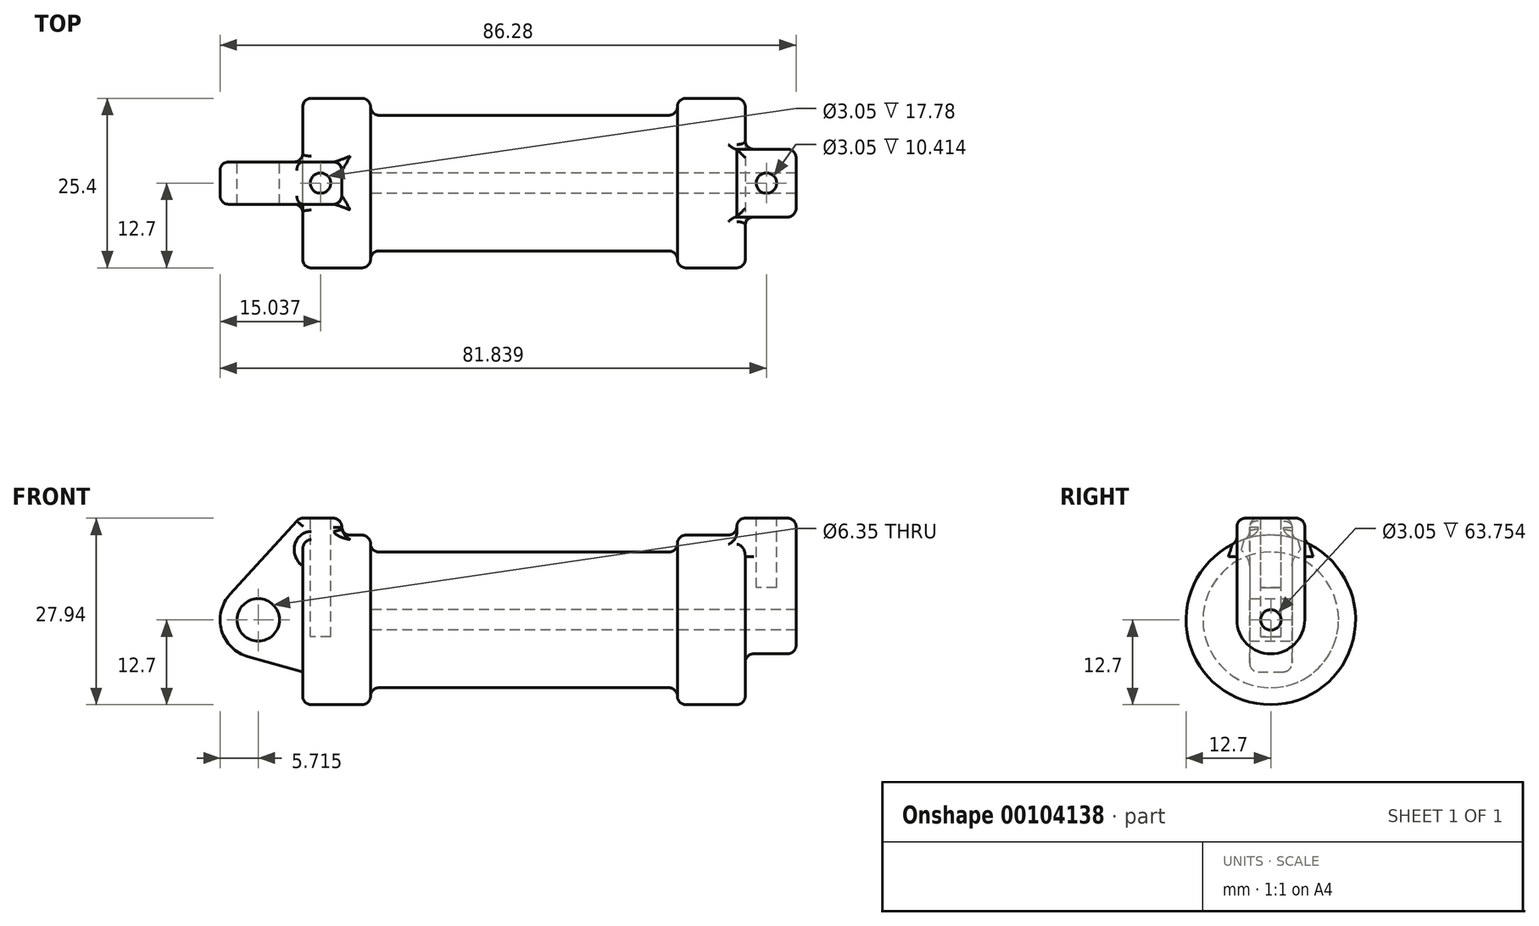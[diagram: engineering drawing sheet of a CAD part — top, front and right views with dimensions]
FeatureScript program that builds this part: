
annotation { "Feature Type Name" : "Feature", "Feature Type Description" : "" }
export const myFeature = defineFeature(function(context is Context, id is Id, definition is map)
    precondition{}
    {
        {
            var Q0;
            Q0=qCreatedBy(makeId("Front.planeOp"),FACE);
            var sketch = newSketch(context, id + "F0", { "sketchPlane" : qUnion([Q0])});
            skLineSegment(sketch, "E0", {"start": v(0, 0) * mm, "end": v(0, 12.7) * mm});
            skLineSegment(sketch, "E1", {"start": v(0, 12.7) * mm, "end": v(10.16, 12.7) * mm});
            skLineSegment(sketch, "E2", {"start": v(10.16, 12.7) * mm, "end": v(10.16, 10.16) * mm});
            skLineSegment(sketch, "E3", {"start": v(10.16, 10.16) * mm, "end": v(56.13, 10.16) * mm});
            skLineSegment(sketch, "E4", {"start": v(56.13, 10.16) * mm, "end": v(56.13, 12.7) * mm});
            skLineSegment(sketch, "E5", {"start": v(56.13, 12.7) * mm, "end": v(66.3, 12.7) * mm});
            skLineSegment(sketch, "E6", {"start": v(66.3, 12.7) * mm, "end": v(66.3, 0) * mm});
            skLineSegment(sketch, "E7", {"start": v(66.3, 0) * mm, "end": v(0, 0) * mm});
            skLineSegment(sketch, "E8", {"start": v(5.84, 15.24) * mm, "end": v(-0.5, 15.24) * mm});
            skLineSegment(sketch, "E9", {"start": v(-0.5, 15.24) * mm, "end": v(-10.88, 3.85) * mm});
            skLineSegment(sketch, "E10", {"start": v(0, 0) * mm, "end": v(-6.65, 0) * mm});
            skCircle(sketch, "E11", {"center": v(-6.65, 0) * mm, "radius": 5.72 * mm});
            skCircle(sketch, "E12", {"center": v(-6.65, 0) * mm, "radius": 3.18 * mm});
            skLineSegment(sketch, "E13", {"start": v(5.84, 15.24) * mm, "end": v(5.84, -9.4) * mm});
            skLineSegment(sketch, "E14", {"start": v(5.84, -9.4) * mm, "end": v(-8.18, -5.5) * mm});
            skSolve(sketch);
        }
        {
            var Q0;
            {var subQ0=sQuery(id+"F0.wireOp",EDGE,"E2");Q0=makeQuery(id+"F0.imprint","IMPRINT",FACE,{"disambiguationData":[TD([[makeQuery(id+"F0.imprint","IMPRINT",EDGE,{"derivedFrom":subQ0}),-1.0]])]});}
            var Q1;
            {var subQ0=sQuery(id+"F0.wireOp",EDGE,"E0");Q1=makeQuery(id+"F0.imprint","IMPRINT",FACE,{"disambiguationData":[TD([[makeQuery(id+"F0.imprint","IMPRINT",EDGE,{"derivedFrom":subQ0}),-1.0]])]});}
            var Q2;
            Q2=sQuery(id+"F0.wireOp",EDGE,"E7");
            revolve(context, id + "F1", {"entities" : qUnion([Q0, Q1]), "axis" : qUnion([Q2]), "revolveType" : RevolveType.FULL});
        }
        {
            var Q0;
            {var subQ3=sQuery(id+"F0.wireOp",EDGE,"E0");Q0=makeQuery(id+"F0.imprint","IMPRINT",FACE,{"disambiguationData":[TD([[makeQuery(id+"F0.imprint","IMPRINT",EDGE,{"derivedFrom":subQ3}),1.0]])]});}
            var Q1;
            {var subQ0=sQuery(id+"F0.wireOp",EDGE,"E0");Q1=makeQuery(id+"F0.imprint","IMPRINT",FACE,{"disambiguationData":[TD([[makeQuery(id+"F0.imprint","IMPRINT",EDGE,{"derivedFrom":subQ0}),-1.0]])]});}
            var Q2;
            {var subQ0=sQuery(id+"F0.wireOp",EDGE,"E14");Q2=makeQuery(id+"F0.imprint","IMPRINT",FACE,{"disambiguationData":[TD([[makeQuery(id+"F0.imprint","IMPRINT",EDGE,{"derivedFrom":subQ0}),-1.0]])]});}
            var Q3;
            {var subQ4=sQuery(id+"F0.wireOp",EDGE,"E12");Q3=makeQuery(id+"F0.imprint","IMPRINT",FACE,{"disambiguationData":[TD([[makeQuery(id+"F0.imprint","IMPRINT",EDGE,{"derivedFrom":subQ4}),-1.0]])]});}
            extrude(context, id + "F2", {"entities" : qUnion([Q0, Q1, Q2, Q3]), "operationType" : NewBodyOperationType.ADD, "depth" : 3.17 * mm});
        }
        {
            var Q0;
            {var subQ4=sQuery(id+"F0.wireOp",EDGE,"E12");Q0=makeQuery(id+"F0.imprint","IMPRINT",FACE,{"disambiguationData":[TD([[makeQuery(id+"F0.imprint","IMPRINT",EDGE,{"derivedFrom":subQ4}),-1.0]])]});}
            var Q1;
            {var subQ3=sQuery(id+"F0.wireOp",EDGE,"E0");Q1=makeQuery(id+"F0.imprint","IMPRINT",FACE,{"disambiguationData":[TD([[makeQuery(id+"F0.imprint","IMPRINT",EDGE,{"derivedFrom":subQ3}),1.0]])]});}
            var Q2;
            {var subQ0=sQuery(id+"F0.wireOp",EDGE,"E0");Q2=makeQuery(id+"F0.imprint","IMPRINT",FACE,{"disambiguationData":[TD([[makeQuery(id+"F0.imprint","IMPRINT",EDGE,{"derivedFrom":subQ0}),-1.0]])]});}
            var Q3;
            {var subQ0=sQuery(id+"F0.wireOp",EDGE,"E14");Q3=makeQuery(id+"F0.imprint","IMPRINT",FACE,{"disambiguationData":[TD([[makeQuery(id+"F0.imprint","IMPRINT",EDGE,{"derivedFrom":subQ0}),-1.0]])]});}
            extrude(context, id + "F3", {"entities" : qUnion([Q0, Q1, Q2, Q3]), "operationType" : NewBodyOperationType.ADD, "oppositeDirection" : true, "depth" : 3.17 * mm});
        }
        {
            var Q0;
            Q0=makeQuery(id+"F1.opRevolve","SWEPT_FACE",FACE,{"disambiguationData":[OSD([sQuery(id+"F0.wireOp",EDGE,"E6")])]});
            var sketch = newSketch(context, id + "F4", { "sketchPlane" : qUnion([Q0])});
            skCircle(sketch, "E15", {"center": v(0, 0) * mm, "radius": 5.08 * mm});
            skCircle(sketch, "E16", {"center": v(0, 0) * mm, "radius": 1.52 * mm});
            skLineSegment(sketch, "E17", {"start": v(-5.08, 0) * mm, "end": v(-5.08, 15.24) * mm});
            skLineSegment(sketch, "E18", {"start": v(-5.08, 15.24) * mm, "end": v(5.08, 15.24) * mm});
            skLineSegment(sketch, "E19", {"start": v(5.08, 15.24) * mm, "end": v(5.08, 0) * mm});
            skSolve(sketch);
        }
        {
            var Q0;
            {var subQ0=sQuery(id+"F4.wireOp",EDGE,"E18");Q0=makeQuery(id+"F4.imprint","IMPRINT",FACE,{"disambiguationData":[TD([[makeQuery(id+"F4.imprint","IMPRINT",EDGE,{"derivedFrom":subQ0}),-1.0]])]});}
            var Q1;
            {var subQ0=sQuery(id+"F4.wireOp",EDGE,"E17");var subQ1=sQuery(id+"F4.wireOp",EDGE,"E15");var subQ2=makeQuery(id+"F4.imprint","INTERSECT",VERTEX,{"derivedFrom":[subQ1,subQ0]});Q1=makeQuery(id+"F4.imprint","IMPRINT",FACE,{"disambiguationData":[TD([[makeQuery(id+"F4.imprint","IMPRINT",EDGE,{"disambiguationData":[TD([[subQ2,1.0]])],"derivedFrom":subQ1}),-1.0]])]});}
            var Q2;
            Q2=makeQuery(id+"F4.imprint","IMPRINT",FACE,{"disambiguationData":[TD([[makeQuery(id+"F4.imprint","IMPRINT",EDGE,{"derivedFrom":sQuery(id+"F4.wireOp",EDGE,"E16")}),-1.0]])]});
            extrude(context, id + "F5", {"entities" : qUnion([Q0, Q1, Q2]), "operationType" : NewBodyOperationType.ADD, "depth" : 7.62 * mm});
        }
        {
            var Q0;
            Q0=makeQuery(id+"F5.opExtrude","CAP_FACE",FACE,{"disambiguationData":[OSD([sQuery(id+"F4.wireOp",EDGE,"E15"),sQuery(id+"F4.wireOp",EDGE,"E16"),sQuery(id+"F4.wireOp",EDGE,"E17"),sQuery(id+"F4.wireOp",EDGE,"E18"),sQuery(id+"F4.wireOp",EDGE,"E19")])],"isStart":false});
            extrude(context, id + "F6", {"entities" : qUnion([Q0]), "operationType" : NewBodyOperationType.ADD, "oppositeDirection" : true, "depth" : 8.9 * mm});
        }
        {
            var Q0;
            {var subQ0=sQuery(id+"F0.wireOp",EDGE,"E8");Q0=makeQuery(id+"F3.boolean.opBoolean","MERGE",FACE,{"derivedFrom":[makeQuery(id+"F2.opExtrude","SWEPT_FACE",FACE,{"disambiguationData":[OSD([subQ0])]}),makeQuery(id+"F3.opExtrude","SWEPT_FACE",FACE,{"disambiguationData":[OSD([subQ0])]})]});}
            var sketch = newSketch(context, id + "F7", { "sketchPlane" : qUnion([Q0])});
            skCircle(sketch, "E20", {"center": v(2.67, 0) * mm, "radius": 1.52 * mm});
            skPoint(sketch, "E20.centerSnap0", {"position": v(5.84, 0) * mm});
            skLineSegment(sketch, "E21.bottom", {"start": v(-0.5, -3.18) * mm, "end": v(2.67, -3.18) * mm, "construction": true});
            skLineSegment(sketch, "E21.top", {"start": v(-0.5, 0) * mm, "end": v(2.67, 0) * mm, "construction": true});
            skLineSegment(sketch, "E21.left", {"start": v(-0.5, -3.18) * mm, "end": v(-0.5, 0) * mm, "construction": true});
            skLineSegment(sketch, "E21.right", {"start": v(2.67, -3.18) * mm, "end": v(2.67, 0) * mm, "construction": true});
            skSolve(sketch);
        }
        {
            var Q0;
            Q0=makeQuery(id+"F7.imprint","IMPRINT",FACE,{"disambiguationData":[TD([[makeQuery(id+"F7.imprint","IMPRINT",EDGE,{"derivedFrom":sQuery(id+"F7.wireOp",EDGE,"E20")}),1.0]])]});
            extrude(context, id + "F8", {"entities" : qUnion([Q0]), "operationType" : NewBodyOperationType.REMOVE, "oppositeDirection" : true, "depth" : 17.78 * mm});
        }
        {
            var Q0;
            {var subQ0=sQuery(id+"F4.wireOp",EDGE,"E18");Q0=makeQuery(id+"F6.boolean.opBoolean","MERGE",FACE,{"derivedFrom":[makeQuery(id+"F5.opExtrude","SWEPT_FACE",FACE,{"disambiguationData":[OSD([subQ0])]}),makeQuery(id+"F6.opExtrude","SWEPT_FACE",FACE,{"disambiguationData":[OSD([subQ0])]})]});}
            var sketch = newSketch(context, id + "F9", { "sketchPlane" : qUnion([Q0])});
            skLineSegment(sketch, "E22.bottom", {"start": v(65.02, -5.08) * mm, "end": v(69.47, -5.08) * mm, "construction": true});
            skLineSegment(sketch, "E22.top", {"start": v(65.02, 0) * mm, "end": v(69.47, 0) * mm, "construction": true});
            skLineSegment(sketch, "E22.left", {"start": v(65.02, -5.08) * mm, "end": v(65.02, 0) * mm, "construction": true});
            skLineSegment(sketch, "E22.right", {"start": v(69.47, -5.08) * mm, "end": v(69.47, 0) * mm, "construction": true});
            skCircle(sketch, "E23", {"center": v(69.47, 0) * mm, "radius": 1.52 * mm});
            skSolve(sketch);
        }
        {
            var Q0;
            Q0=makeQuery(id+"F9.imprint","IMPRINT",FACE,{"disambiguationData":[TD([[makeQuery(id+"F9.imprint","IMPRINT",EDGE,{"derivedFrom":sQuery(id+"F9.wireOp",EDGE,"E23")}),1.0]])]});
            extrude(context, id + "F10", {"entities" : qUnion([Q0]), "operationType" : NewBodyOperationType.REMOVE, "oppositeDirection" : true, "depth" : 10.4 * mm});
        }
        {
            var Q0;
            Q0=makeQuery(id+"F1.opRevolve","SWEPT_EDGE",EDGE,{"disambiguationData":[OSD([sQuery(id+"F0.wireOp",EDGE,"E1"),sQuery(id+"F0.wireOp",EDGE,"E2")])]});
            var Q1;
            Q1=makeQuery(id+"F1.opRevolve","SWEPT_EDGE",EDGE,{"disambiguationData":[OSD([sQuery(id+"F0.wireOp",EDGE,"E0"),sQuery(id+"F0.wireOp",EDGE,"E1")])]});
            var Q2;
            Q2=makeQuery(id+"F1.opRevolve","SWEPT_EDGE",EDGE,{"disambiguationData":[OSD([sQuery(id+"F0.wireOp",EDGE,"E4"),sQuery(id+"F0.wireOp",EDGE,"E5")])]});
            var Q3;
            Q3=makeQuery(id+"F5.boolean.opBoolean","SPLIT",EDGE,{"disambiguationData":[OD(1.0)],"derivedFrom":makeQuery(id+"F1.opRevolve","SWEPT_EDGE",EDGE,{"disambiguationData":[OSD([sQuery(id+"F0.wireOp",EDGE,"E5"),sQuery(id+"F0.wireOp",EDGE,"E6")])]})});
            var Q4;
            Q4=makeQuery(id+"F5.opExtrude","CAP_EDGE",EDGE,{"disambiguationData":[OSD([sQuery(id+"F4.wireOp",EDGE,"E15")])],"isStart":false});
            var Q5;
            Q5=makeQuery(id+"F2.opExtrude","CAP_EDGE",EDGE,{"disambiguationData":[OSD([sQuery(id+"F0.wireOp",EDGE,"E11")])],"isStart":false});
            var Q6;
            Q6=makeQuery(id+"F3.opExtrude","CAP_EDGE",EDGE,{"disambiguationData":[OSD([sQuery(id+"F0.wireOp",EDGE,"E11")])],"isStart":false});
            var Q7;
            {var subQ0=sQuery(id+"F4.wireOp",EDGE,"E18");var subQ1=sQuery(id+"F4.wireOp",EDGE,"E17");Q7=makeQuery(id+"F6.boolean.opBoolean","MERGE",EDGE,{"derivedFrom":[makeQuery(id+"F5.opExtrude","SWEPT_EDGE",EDGE,{"disambiguationData":[OSD([subQ1,subQ0])]}),makeQuery(id+"F6.opExtrude","SWEPT_EDGE",EDGE,{"disambiguationData":[OSD([subQ1,subQ0])]})]});}
            var Q8;
            Q8=makeQuery(id+"F5.opExtrude","CAP_EDGE",EDGE,{"disambiguationData":[OSD([sQuery(id+"F4.wireOp",EDGE,"E18")])],"isStart":false});
            var Q9;
            Q9=makeQuery(id+"F6.opExtrude","CAP_EDGE",EDGE,{"disambiguationData":[OSD([sQuery(id+"F4.wireOp",EDGE,"E18")])],"isStart":false});
            var Q10;
            {var subQ0=sQuery(id+"F4.wireOp",EDGE,"E19");var subQ1=sQuery(id+"F4.wireOp",EDGE,"E18");Q10=makeQuery(id+"F6.boolean.opBoolean","MERGE",EDGE,{"derivedFrom":[makeQuery(id+"F5.opExtrude","SWEPT_EDGE",EDGE,{"disambiguationData":[OSD([subQ1,subQ0])]}),makeQuery(id+"F6.opExtrude","SWEPT_EDGE",EDGE,{"disambiguationData":[OSD([subQ1,subQ0])]})]});}
            var Q11;
            Q11=makeQuery(id+"F3.opExtrude","CAP_EDGE",EDGE,{"disambiguationData":[OSD([sQuery(id+"F0.wireOp",EDGE,"E8")])],"isStart":false});
            var Q12;
            Q12=makeQuery(id+"F2.opExtrude","CAP_EDGE",EDGE,{"disambiguationData":[OSD([sQuery(id+"F0.wireOp",EDGE,"E8")])],"isStart":false});
            var Q13;
            Q13=makeQuery(id+"F3.boolean.opBoolean","INTERSECT",EDGE,{"derivedFrom":[makeQuery(id+"F1.opRevolve","SWEPT_FACE",FACE,{"disambiguationData":[OSD([sQuery(id+"F0.wireOp",EDGE,"E1")])]}),makeQuery(id+"F3.opExtrude","SWEPT_FACE",FACE,{"disambiguationData":[OSD([sQuery(id+"F0.wireOp",EDGE,"E13")])]})]});
            var Q14;
            Q14=makeQuery(id+"F2.boolean.opBoolean","INTERSECT",EDGE,{"derivedFrom":[makeQuery(id+"F1.opRevolve","SWEPT_FACE",FACE,{"disambiguationData":[OSD([sQuery(id+"F0.wireOp",EDGE,"E1")])]}),makeQuery(id+"F2.opExtrude","CAP_FACE",FACE,{"disambiguationData":[OSD([sQuery(id+"F0.wireOp",EDGE,"E8"),sQuery(id+"F0.wireOp",EDGE,"E9"),sQuery(id+"F0.wireOp",EDGE,"E11"),sQuery(id+"F0.wireOp",EDGE,"E12"),sQuery(id+"F0.wireOp",EDGE,"E13"),sQuery(id+"F0.wireOp",EDGE,"E14")])],"isStart":false})]});
            var Q15;
            Q15=makeQuery(id+"F3.boolean.opBoolean","INTERSECT",EDGE,{"derivedFrom":[makeQuery(id+"F1.opRevolve","SWEPT_FACE",FACE,{"disambiguationData":[OSD([sQuery(id+"F0.wireOp",EDGE,"E1")])]}),makeQuery(id+"F3.opExtrude","CAP_FACE",FACE,{"disambiguationData":[OSD([sQuery(id+"F0.wireOp",EDGE,"E8"),sQuery(id+"F0.wireOp",EDGE,"E9"),sQuery(id+"F0.wireOp",EDGE,"E11"),sQuery(id+"F0.wireOp",EDGE,"E12"),sQuery(id+"F0.wireOp",EDGE,"E13"),sQuery(id+"F0.wireOp",EDGE,"E14")])],"isStart":false})]});
            fillet(context, id + "F11", {"entities" : qUnion([Q0, Q1, Q2, Q3, Q4, Q5, Q6, Q7, Q8, Q9, Q10, Q11, Q12, Q13, Q14, Q15]), "radius" : 1.27 * mm, "tangentPropagation" : true, "allowEdgeOverflow" : false});
        }
        {
            var Q0;
            {var subQ0=sQuery(id+"F4.wireOp",EDGE,"E17");var subQ1=sQuery(id+"F4.wireOp",EDGE,"E15");Q0=makeQuery(id+"F5.boolean.opBoolean","SPLIT",EDGE,{"disambiguationData":[TD([makeQuery(id+"F5.opExtrude","SWEPT_FACE",FACE,{"disambiguationData":[OSD([subQ1])]})])],"derivedFrom":makeQuery(id+"F5.opExtrude","CAP_EDGE",EDGE,{"disambiguationData":[OSD([subQ0])],"isStart":true})});}
            var Q1;
            Q1=makeQuery(id+"F5.opExtrude","CAP_EDGE",EDGE,{"disambiguationData":[OSD([sQuery(id+"F4.wireOp",EDGE,"E15")])],"isStart":true});
            var Q2;
            {var subQ0=sQuery(id+"F0.wireOp",EDGE,"E9");var subQ1=sQuery(id+"F0.wireOp",EDGE,"E8");Q2=makeQuery(id+"F3.boolean.opBoolean","MERGE",EDGE,{"derivedFrom":[makeQuery(id+"F2.opExtrude","SWEPT_EDGE",EDGE,{"disambiguationData":[OSD([subQ1,subQ0])]}),makeQuery(id+"F3.opExtrude","SWEPT_EDGE",EDGE,{"disambiguationData":[OSD([subQ1,subQ0])]})]});}
            var Q3;
            Q3=makeQuery(id+"F6.boolean.opBoolean","INTERSECT",EDGE,{"derivedFrom":[makeQuery(id+"F1.opRevolve","SWEPT_FACE",FACE,{"disambiguationData":[OSD([sQuery(id+"F0.wireOp",EDGE,"E5")])]}),makeQuery(id+"F6.opExtrude","CAP_FACE",FACE,{"disambiguationData":[OSD([sQuery(id+"F4.wireOp",EDGE,"E15"),sQuery(id+"F4.wireOp",EDGE,"E16"),sQuery(id+"F4.wireOp",EDGE,"E17"),sQuery(id+"F4.wireOp",EDGE,"E18"),sQuery(id+"F4.wireOp",EDGE,"E19")])],"isStart":false})]});
            var Q4;
            {var subQ0=sQuery(id+"F0.wireOp",EDGE,"E13");var subQ1=makeQuery(id+"F3.opExtrude","SWEPT_FACE",FACE,{"disambiguationData":[OSD([subQ0])]});Q4=makeQuery(id+"F11.opFillet","BLEND_EDGE",EDGE,{"blendedFrom":[makeQuery(id+"F3.boolean.opBoolean","INTERSECT",EDGE,{"derivedFrom":[makeQuery(id+"F1.opRevolve","SWEPT_FACE",FACE,{"disambiguationData":[OSD([sQuery(id+"F0.wireOp",EDGE,"E1")])]}),subQ1]}),makeQuery(id+"F3.boolean.opBoolean","MERGE",FACE,{"derivedFrom":[makeQuery(id+"F2.opExtrude","SWEPT_FACE",FACE,{"disambiguationData":[OSD([subQ0])]}),subQ1]})],"blendedInto":[makeQuery(id+"F3.boolean.opBoolean","MERGE",FACE,{"derivedFrom":[makeQuery(id+"F2.opExtrude","SWEPT_FACE",FACE,{"disambiguationData":[OSD([subQ0])]}),subQ1]})]});}
            var Q5;
            {var subQ0=sQuery(id+"F0.wireOp",EDGE,"E13");var subQ1=sQuery(id+"F0.wireOp",EDGE,"E8");Q5=makeQuery(id+"F3.boolean.opBoolean","MERGE",EDGE,{"derivedFrom":[makeQuery(id+"F2.opExtrude","SWEPT_EDGE",EDGE,{"disambiguationData":[OSD([subQ1,subQ0])]}),makeQuery(id+"F3.opExtrude","SWEPT_EDGE",EDGE,{"disambiguationData":[OSD([subQ1,subQ0])]})]});}
            var Q6;
            Q6=makeQuery(id+"F1.opRevolve","SWEPT_EDGE",EDGE,{"disambiguationData":[OSD([sQuery(id+"F0.wireOp",EDGE,"E3"),sQuery(id+"F0.wireOp",EDGE,"E4")])]});
            fillet(context, id + "F12", {"entities" : qUnion([Q0, Q1, Q2, Q3, Q4, Q5, Q6]), "radius" : 1.27 * mm, "tangentPropagation" : true, "allowEdgeOverflow" : false});
        }
        {
            var Q0;
            Q0=makeQuery(id+"F5.boolean.opBoolean","SPLIT",FACE,{"disambiguationData":[TD([makeQuery(id+"F5.opExtrude","SWEPT_FACE",FACE,{"disambiguationData":[OSD([sQuery(id+"F4.wireOp",EDGE,"E16")])]})])],"derivedFrom":makeQuery(id+"F1.opRevolve","SWEPT_FACE",FACE,{"disambiguationData":[OSD([sQuery(id+"F0.wireOp",EDGE,"E6")])]})});
            var Q1;
            Q1=makeQuery(id+"F1.opRevolve","SWEPT_FACE",FACE,{"disambiguationData":[OSD([sQuery(id+"F0.wireOp",EDGE,"E2")])]});
            extrude(context, id + "F13", {"entities" : qUnion([Q0]), "operationType" : NewBodyOperationType.REMOVE, "endBound" : BoundingType.UP_TO_SURFACE, "oppositeDirection" : true, "endBoundEntityFace" : qUnion([Q1]), "depth" : 25.4 * mm});
        }
        {
            var Q0;
            Q0=makeQuery(id+"F1.opRevolve","SWEPT_EDGE",EDGE,{"disambiguationData":[OSD([sQuery(id+"F0.wireOp",EDGE,"E2"),sQuery(id+"F0.wireOp",EDGE,"E3")])]});
            fillet(context, id + "F14", {"entities" : qUnion([Q0]), "radius" : 1.27 * mm, "tangentPropagation" : true, "allowEdgeOverflow" : false});
        }
    });
